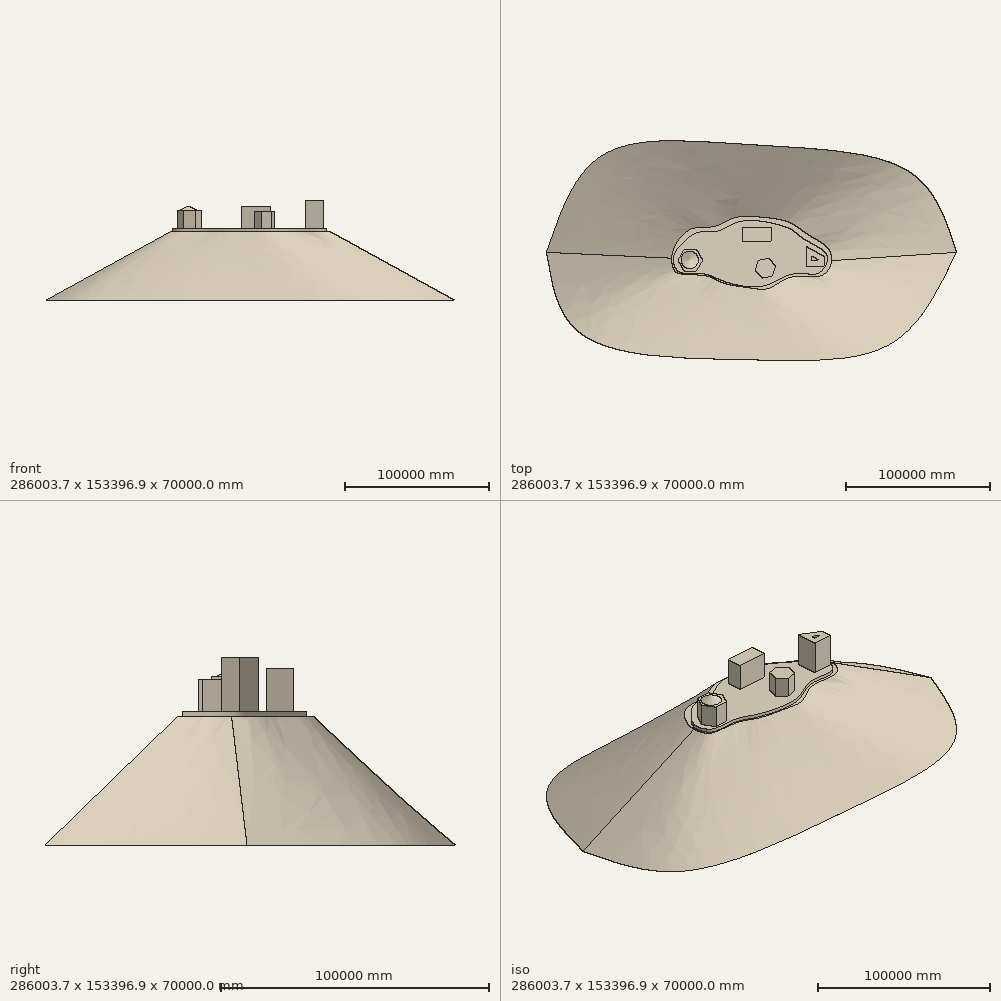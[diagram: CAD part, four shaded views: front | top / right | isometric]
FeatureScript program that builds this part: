
annotation { "Feature Type Name" : "Feature", "Feature Type Description" : "" }
export const myFeature = defineFeature(function(context is Context, id is Id, definition is map)
    precondition{}
    {
        {
            var Q0;
            Q0=qCreatedBy(makeId("Top.planeOp"),FACE);
            var sketch = newSketch(context, id + "F0", { "sketchPlane" : qUnion([Q0])});
            skFitSpline(sketch, "E0", {"points": [v(-143001.83, 0) * mm, v(-103603.63, 67775.48) * mm, v(0, 75000) * mm, v(111116.53, 55565.9) * mm, v(143001.83, 0) * mm], "startDerivative": vector(119090.8, 351106.87) * mm, "endDerivative": vector(96155.49, -304758.65) * mm});
            skFitSpline(sketch, "E1", {"points": [v(-143001.83, 0) * mm, v(-118760.35, -56846.41) * mm, v(0, -75000) * mm, v(98485.93, -63161.72) * mm, v(143001.83, 0) * mm], "startDerivative": vector(50450.26, -316321.73) * mm, "endDerivative": vector(152462.47, 323683.6) * mm});
            skSolve(sketch);
        }
        {
            var Q0;
            Q0=qCreatedBy(makeId("Top.planeOp"),FACE);
            cPlane(context, id + "F1", {"entities" : qUnion([Q0]), "cplaneType" : CPlaneType.OFFSET, "offset" : 48000 * mm, "width" : 150 * mm, "height" : 150 * mm});
        }
        {
            var Q0;
            Q0=qCreatedBy(id+"F1.planeOp",FACE);
            var sketch = newSketch(context, id + "F2", { "sketchPlane" : qUnion([Q0])});
            skFitSpline(sketch, "E2", {"points": [v(-55000, 0) * mm, v(-42253.62, 16006.7) * mm, v(-25722.82, 17990.39) * mm, v(-13159.41, 23610.86) * mm, v(0, 25000) * mm, v(26183.88, 20965.93) * mm, v(39408.52, 12369.92) * mm, v(55000, 0) * mm, v(50649.47, -15401.82) * mm, v(28828.81, -17054.9) * mm, v(12628.63, -24989.68) * mm, v(0, -25000) * mm, v(-20763.58, -21022.3) * mm, v(-31673.9, -16393.67) * mm, v(-51510.86, -14409.97) * mm, v(-55000, -9781.35) * mm, v(-55000, 0) * mm]});
            skSolve(sketch);
        }
        {
            var Q0;
            Q0=makeQuery(id+"F2.imprint","IMPRINT",FACE,{"disambiguationData":[TD([[makeQuery(id+"F2.imprint","IMPRINT",EDGE,{"derivedFrom":sQuery(id+"F2.wireOp",EDGE,"E2")}),-1.0]])]});
            var Q1;
            Q1=makeQuery(id+"F0.imprint","IMPRINT",FACE,{"disambiguationData":[TD([[makeQuery(id+"F0.imprint","IMPRINT",EDGE,{"derivedFrom":sQuery(id+"F0.wireOp",EDGE,"E0")}),-1.0]])]});
            loft(context, id + "F3", {"sheetProfilesArray" : [{ "sheetProfileEntities" : qUnion([Q0]) }, { "sheetProfileEntities" : qUnion([Q1]) }]});
        }
        {
            var Q0;
            Q0=makeQuery(id+"F3.opLoft","CAP_FACE",FACE,{"disambiguationData":[OSD([makeQuery(id+"F2.imprint","IMPRINT",FACE,{"disambiguationData":[TD([[makeQuery(id+"F2.imprint","IMPRINT",EDGE,{"derivedFrom":sQuery(id+"F2.wireOp",EDGE,"E2")}),-1.0]])]})])],"isStart":true});
            var sketch = newSketch(context, id + "F4", { "sketchPlane" : qUnion([Q0])});
            skLineSegment(sketch, "E3.0", {"start": v(-46900.84, 1856.44) * mm, "end": v(-38240.59, 1856.44) * mm});
            skLineSegment(sketch, "E3.1", {"start": v(-38240.59, 1856.44) * mm, "end": v(-33910.46, -5643.56) * mm});
            skLineSegment(sketch, "E3.2", {"start": v(-33910.46, -5643.56) * mm, "end": v(-38240.59, -13143.56) * mm});
            skLineSegment(sketch, "E3.3", {"start": v(-38240.59, -13143.56) * mm, "end": v(-46900.84, -13143.56) * mm});
            skLineSegment(sketch, "E3.4", {"start": v(-46900.84, -13143.56) * mm, "end": v(-51230.97, -5643.56) * mm});
            skLineSegment(sketch, "E3.5", {"start": v(-51230.97, -5643.56) * mm, "end": v(-46900.84, 1856.44) * mm});
            skPoint(sketch, "E3.0.midPoint", {"position": v(-42570.72, 1856.44) * mm});
            skSolve(sketch);
        }
        {
            var Q0;
            Q0=makeQuery(id+"F4.imprint","IMPRINT",FACE,{"disambiguationData":[TD([[makeQuery(id+"F4.imprint","IMPRINT",EDGE,{"derivedFrom":sQuery(id+"F4.wireOp",EDGE,"E3.0")}),-1.0]])]});
            extrude(context, id + "F5", {"entities" : qUnion([Q0]), "operationType" : NewBodyOperationType.ADD, "depth" : 15000 * mm});
        }
        {
            var Q0;
            Q0=makeQuery(id+"F3.opLoft","CAP_FACE",FACE,{"disambiguationData":[OSD([makeQuery(id+"F2.imprint","IMPRINT",FACE,{"disambiguationData":[TD([[makeQuery(id+"F2.imprint","IMPRINT",EDGE,{"derivedFrom":sQuery(id+"F2.wireOp",EDGE,"E2")}),-1.0]])]})])],"isStart":true});
            var sketch = newSketch(context, id + "F6", { "sketchPlane" : qUnion([Q0])});
            skFitSpline(sketch, "E4", {"points": [v(-54539.07, -4369.4) * mm, v(-53149.78, -10690.65) * mm, v(-49607.1, -14024.93) * mm, v(-40159.98, -14719.57) * mm, v(-30296.07, -15622.6) * mm, v(-20223.76, -19859.92) * mm, v(4991.73, -24027.77) * mm, v(19996, -18817.96) * mm, v(31519.21, -14714.38) * mm, v(45049.44, -15130.7) * mm, v(50773.76, -11071.63) * mm, v(52855.34, -2433.1) * mm, v(44945.35, 4540.17) * mm, v(35266.04, 10160.42) * mm, v(28709.09, 15364.35) * mm, v(18925.7, 19319.34) * mm, v(4042.44, 22025.38) * mm, v(-9279.62, 21088.68) * mm, v(-18958.94, 16405.14) * mm, v(-24371.03, 14739.88) * mm, v(-34674.82, 14427.64) * mm, v(-43209.27, 10680.81) * mm, v(-48829.52, 5164.64) * mm, v(-51431.48, 2458.6) * mm, v(-54539.07, -4369.4) * mm]});
            skFitSpline(sketch, "E5.0", {"points": [v(-53544.52, -4476.42) * mm, v(-53547.52, -4499.05) * mm, v(-53550.44, -4521.66) * mm, v(-53554.23, -4551.8) * mm, v(-53558.8, -4589.44) * mm, v(-53564, -4634.58) * mm, v(-53570.55, -4694.73) * mm, v(-53578.03, -4769.84) * mm, v(-53585.88, -4859.82) * mm, v(-53592.64, -4949.67) * mm, v(-53600.18, -5069.29) * mm, v(-53606.92, -5218.46) * mm, v(-53610.77, -5396.9) * mm, v(-53610.48, -5574.73) * mm, v(-53606.15, -5751.95) * mm, v(-53595.12, -5987.4) * mm, v(-53571.67, -6280.03) * mm, v(-53528.82, -6628.25) * mm, v(-53471.97, -6973.25) * mm, v(-53401.87, -7314.66) * mm, v(-53319.26, -7652.1) * mm, v(-53224.9, -7985.19) * mm, v(-53119.6, -8313.47) * mm, v(-53004.11, -8636.52) * mm, v(-52879.3, -8953.87) * mm, v(-52768.19, -9213.19) * mm, v(-52675.48, -9417.32) * mm, v(-52604.15, -9568.7) * mm, v(-52531.13, -9718.31) * mm, v(-52456.52, -9866.08) * mm, v(-52393.12, -9987.64) * mm, v(-52348.14, -10071.87) * mm, v(-52322.28, -10119.76) * mm, v(-52302.8, -10155.55) * mm, v(-52283.25, -10191.2) * mm, v(-52263.62, -10226.75) * mm, v(-52243.95, -10262.1) * mm, v(-52217.66, -10308.96) * mm, v(-52184.7, -10367.08) * mm, v(-52144.94, -10436.05) * mm, v(-52105, -10504.25) * mm, v(-52051.47, -10594.15) * mm, v(-51984.03, -10704.58) * mm, v(-51902.17, -10833.96) * mm, v(-51819.32, -10960.18) * mm, v(-51735.4, -11083.23) * mm, v(-51650.35, -11203.1) * mm, v(-51564.1, -11319.77) * mm, v(-51447.36, -11471.1) * mm, v(-51298.03, -11652.32) * mm, v(-51112.66, -11857.28) * mm, v(-50920.31, -12049.98) * mm, v(-50720.03, -12230.77) * mm, v(-50510.68, -12400.03) * mm, v(-50327.6, -12531.8) * mm, v(-50175.22, -12631.77) * mm, v(-50057.8, -12704.07) * mm, v(-49937.03, -12773.7) * mm, v(-49812.7, -12840.67) * mm, v(-49705.98, -12894.26) * mm, v(-49618.61, -12935.8) * mm, v(-49552.07, -12966.28) * mm, v(-49484.49, -12996.1) * mm, v(-49415.83, -13025.22) * mm, v(-49357.71, -13048.93) * mm, v(-49310.65, -13067.56) * mm, v(-49281, -13079.05) * mm, v(-49257.15, -13088.16) * mm, v(-49233.19, -13097.22) * mm, v(-49203, -13108.45) * mm, v(-49166.44, -13121.77) * mm, v(-49117.22, -13139.34) * mm, v(-49054.8, -13160.92) * mm, v(-48978.54, -13186.22) * mm, v(-48900.9, -13210.91) * mm, v(-48795.58, -13243.02) * mm, v(-48660.6, -13281.64) * mm, v(-48493.46, -13325.52) * mm, v(-48321.32, -13366.96) * mm, v(-48144.34, -13405.96) * mm, v(-47902.13, -13454.74) * mm, v(-47588.1, -13509.74) * mm, v(-47194.53, -13566.53) * mm, v(-46785.56, -13614.53) * mm, v(-46362.45, -13654.23) * mm, v(-45926.46, -13686.23) * mm, v(-45478.78, -13711.12) * mm, v(-45020.6, -13729.57) * mm, v(-44553.06, -13742.26) * mm, v(-44077.28, -13749.9) * mm, v(-43594.36, -13753.22) * mm, v(-43105.36, -13752.94) * mm, v(-42611.34, -13749.83) * mm, v(-42113.32, -13744.64) * mm, v(-41695.81, -13739.23) * mm, v(-41360.8, -13734.64) * mm, v(-41109.17, -13731.16) * mm, v(-40857.28, -13727.75) * mm, v(-40647.26, -13725.04) * mm, v(-40479.23, -13723) * mm, v(-40353.22, -13721.55) * mm, v(-40227.24, -13720.19) * mm, v(-40059.3, -13718.51) * mm, v(-39849.65, -13716.7) * mm, v(-39598.45, -13715.02) * mm, v(-39347.67, -13713.88) * mm, v(-39013.89, -13713.17) * mm, v(-38597.78, -13713.9) * mm, v(-38100.41, -13717.75) * mm, v(-37605.12, -13725) * mm, v(-37112.05, -13736.03) * mm, v(-36457.76, -13756.36) * mm, v(-35646.1, -13793.3) * mm, v(-34843.58, -13848.4) * mm, v(-34207.58, -13905.07) * mm, v(-33733.72, -13954.32) * mm, v(-33263.13, -14010.74) * mm, v(-32795.95, -14074.77) * mm, v(-32332.31, -14146.87) * mm, v(-31872.37, -14227.5) * mm, v(-31492.3, -14302.16) * mm, v(-31190.24, -14366.62) * mm, v(-30964.72, -14417.38) * mm, v(-30740.25, -14470.62) * mm, v(-30554.07, -14517.1) * mm, v(-30405.68, -14555.58) * mm, v(-30294.66, -14585.1) * mm, v(-30183.91, -14615.28) * mm, v(-30101.07, -14638.42) * mm, v(-30045.93, -14654.06) * mm, v(-30009.19, -14664.55) * mm, v(-29944.98, -14683.03) * mm, v(-29853.55, -14709.83) * mm, v(-29744.25, -14742.61) * mm, v(-29635.37, -14776) * mm, v(-29526.88, -14810) * mm, v(-29382.75, -14856.09) * mm, v(-29203.5, -14915.15) * mm, v(-28989.74, -14988.26) * mm, v(-28777.19, -15063.5) * mm, v(-28565.71, -15140.8) * mm, v(-28285, -15246.51) * mm, v(-27936.1, -15383.4) * mm, v(-27519.5, -15554.63) * mm, v(-27103.8, -15732.24) * mm, v(-26687.8, -15915.66) * mm, v(-26270.27, -16104.35) * mm, v(-25849.97, -16297.79) * mm, v(-25425.65, -16495.5) * mm, v(-24996.03, -16697) * mm, v(-24559.84, -16901.86) * mm, v(-24115.8, -17109.65) * mm, v(-23662.6, -17319.95) * mm, v(-23198.98, -17532.35) * mm, v(-22723.63, -17746.45) * mm, v(-22235.26, -17961.86) * mm, v(-21732.57, -18178.17) * mm, v(-21300.66, -18358.86) * mm, v(-20946.68, -18503.46) * mm, v(-20676.81, -18611.9) * mm, v(-20448.13, -18702.19) * mm, v(-20262.84, -18774.36) * mm, v(-20122.67, -18828.45) * mm, v(-20004.85, -18873.49) * mm, v(-19909.97, -18909.5) * mm, v(-19814.69, -18945.48) * mm, v(-19694.74, -18990.45) * mm, v(-19549.5, -19044.37) * mm, v(-19402.98, -19098.25) * mm, v(-19205.91, -19170.02) * mm, v(-18956.44, -19259.58) * mm, v(-18652.2, -19366.75) * mm, v(-18343.2, -19473.57) * mm, v(-18029.6, -19579.96) * mm, v(-17605.5, -19721.18) * mm, v(-17064.55, -19896.36) * mm, v(-16399.15, -20103.97) * mm, v(-15718.57, -20308.5) * mm, v(-15023.88, -20509.5) * mm, v(-14316.14, -20706.53) * mm, v(-13356.52, -20963.33) * mm, v(-12129.69, -21272.15) * mm, v(-10622.28, -21619.71) * mm, v(-9088.1, -21940.75) * mm, v(-7535.59, -22231.77) * mm, v(-5973.22, -22489.32) * mm, v(-4409.5, -22709.98) * mm, v(-2852.93, -22890.34) * mm, v(-1312.11, -23027.06) * mm, v(-48.45, -23101.87) * mm, v(945.9, -23136.64) * mm, v(1682.28, -23149.8) * mm, v(2287.16, -23149.66) * mm, v(2765.25, -23142.71) * mm, v(3120.78, -23134.04) * mm, v(3473.1, -23121.85) * mm, v(3822.1, -23106.1) * mm, v(4110.05, -23090) * mm, v(4338.6, -23075.28) * mm, v(4509.08, -23063.33) * mm, v(4678.62, -23050.46) * mm, v(4819.11, -23038.97) * mm, v(4931, -23029.3) * mm, v(5042.61, -23019.34) * mm, v(5181.57, -23006.29) * mm, v(5347.46, -22989.7) * mm, v(5567.51, -22966.38) * mm, v(5840.46, -22934.95) * mm, v(6164.67, -22893.7) * mm, v(6592.62, -22834.08) * mm, v(7119.58, -22751.08) * mm, v(7739.7, -22638.52) * mm, v(8348.11, -22513.6) * mm, v(8945.34, -22376.9) * mm, v(9727.39, -22179.73) * mm, v(10679.53, -21906.75) * mm, v(11785.41, -21541.33) * mm, v(12858.52, -21142.64) * mm, v(13902.66, -20715.24) * mm, v(14921.55, -20263.71) * mm, v(15918.89, -19792.7) * mm, v(16898.29, -19306.87) * mm, v(17863.36, -18811) * mm, v(18817.74, -18309.94) * mm, v(19765.04, -17808.57) * mm, v(20708.96, -17311.91) * mm, v(21653.37, -16824.93) * mm, v(22602.15, -16352.73) * mm, v(23559.2, -15900.54) * mm, v(24528.39, -15473.74) * mm, v(25513.51, -15077.84) * mm, v(26350.8, -14778.42) * mm, v(27032.17, -14560.07) * mm, v(27549.39, -14407.65) * mm, v(28073.2, -14267.28) * mm, v(28603.97, -14139.73) * mm, v(29052.4, -14044.7) * mm, v(29414.97, -13975.83) * mm, v(29688.87, -13927.83) * mm, v(29964.77, -13883.57) * mm, v(30242.7, -13843.15) * mm, v(30522.73, -13806.66) * mm, v(30757.84, -13779.59) * mm, v(30947.02, -13759.98) * mm, v(31089.44, -13746.31) * mm, v(31208.58, -13735.8) * mm, v(31304.17, -13727.9) * mm, v(31364.03, -13723.2) * mm, v(31412, -13719.57) * mm, v(31448, -13716.9) * mm, v(31484.03, -13714.32) * mm, v(31532.1, -13710.95) * mm, v(31592.22, -13706.92) * mm, v(31688.53, -13700.81) * mm, v(31809.1, -13693.84) * mm, v(31954.08, -13686.5) * mm, v(32099.32, -13680.14) * mm, v(32293.32, -13672.96) * mm, v(32536.42, -13666.35) * mm, v(32829.02, -13661.97) * mm, v(33122.37, -13660.96) * mm, v(33416.38, -13663.1) * mm, v(33809.12, -13669.9) * mm, v(34301.14, -13685.33) * mm, v(34892.4, -13713.34) * mm, v(35483.6, -13749.34) * mm, v(36073.8, -13791.84) * mm, v(36662.02, -13839.37) * mm, v(37247.28, -13890.45) * mm, v(37828.57, -13943.66) * mm, v(38404.84, -13997.55) * mm, v(38975.02, -14050.72) * mm, v(39538, -14101.73) * mm, v(40092.66, -14149.22) * mm, v(40637.83, -14191.8) * mm, v(41172.28, -14228.1) * mm, v(41694.78, -14256.83) * mm, v(42204.03, -14276.66) * mm, v(42698.68, -14286.36) * mm, v(43097.55, -14285) * mm, v(43407.93, -14277.71) * mm, v(43636.16, -14269) * mm, v(43859.66, -14256.95) * mm, v(44078.22, -14241.42) * mm, v(44256.1, -14225.5) * mm, v(44395.74, -14210.94) * mm, v(44499.12, -14199.09) * mm, v(44601.12, -14186.3) * mm, v(44684.96, -14174.86) * mm, v(44751.32, -14165.23) * mm, v(44800.73, -14157.77) * mm, v(44841.6, -14151.35) * mm, v(44874.13, -14146.1) * mm, v(44906.52, -14140.77) * mm, v(44946.83, -14133.94) * mm, v(44994.9, -14125.5) * mm, v(45042.68, -14116.8) * mm, v(45106, -14104.88) * mm, v(45184.42, -14089.36) * mm, v(45277.39, -14069.74) * mm, v(45369.23, -14049.15) * mm, v(45490.22, -14020.4) * mm, v(45638.76, -13982.05) * mm, v(45812.83, -13932.21) * mm, v(45982.9, -13878.6) * mm, v(46149.13, -13821.25) * mm, v(46365.9, -13739.83) * mm, v(46628.17, -13628.8) * mm, v(46930.35, -13480.83) * mm, v(47221.36, -13318) * mm, v(47502.49, -13140.12) * mm, v(47774.9, -12946.9) * mm, v(48039.66, -12738.03) * mm, v(48297.66, -12513.2) * mm, v(48549.69, -12272.13) * mm, v(48796.42, -12014.58) * mm, v(48998.12, -11786.11) * mm, v(49157.4, -11594.99) * mm, v(49275.87, -11447.47) * mm, v(49393.43, -11295.78) * mm, v(49510.13, -11139.93) * mm, v(49606.7, -11006.6) * mm, v(49683.6, -10897.85) * mm, v(49741.1, -10815.27) * mm, v(49798.41, -10731.66) * mm, v(49855.57, -10647.02) * mm, v(49898.32, -10582.77) * mm, v(49926.78, -10539.62) * mm, v(49945.74, -10510.77) * mm, v(49978.87, -10460.08) * mm, v(50026.03, -10387.13) * mm, v(50082.35, -10298.75) * mm, v(50138.38, -10209.56) * mm, v(50212.64, -10089.57) * mm, v(50304.6, -9937.67) * mm, v(50413.37, -9752.48) * mm, v(50520.37, -9564.58) * mm, v(50660.46, -9310.67) * mm, v(50830.24, -8987.4) * mm, v(51024.06, -8591.52) * mm, v(51206.54, -8189.19) * mm, v(51376.32, -7781.9) * mm, v(51532.07, -7371.16) * mm, v(51672.5, -6958.52) * mm, v(51796.34, -6545.53) * mm, v(51902.42, -6133.77) * mm, v(51989.61, -5724.82) * mm, v(52056.89, -5320.27) * mm, v(52103.31, -4921.7) * mm, v(52123.94, -4595.79) * mm, v(52129.25, -4339.51) * mm, v(52127.57, -4149.7) * mm, v(52120.14, -3962.44) * mm, v(52106.92, -3777.86) * mm, v(52087.83, -3596.1) * mm, v(52062.83, -3417.25) * mm, v(52037, -3270.72) * mm, v(52013.34, -3155.04) * mm, v(51994.07, -3069.05) * mm, v(51973.27, -2983.84) * mm, v(51954.66, -2913.49) * mm, v(51939, -2857.6) * mm, v(51926.88, -2815.88) * mm, v(51916.44, -2781.27) * mm, v(51907.9, -2753.69) * mm, v(51901.4, -2733.05) * mm, v(51894.8, -2712.44) * mm, v(51885.84, -2685) * mm, v(51874.38, -2650.73) * mm, v(51860.2, -2609.69) * mm, v(51840.74, -2555.06) * mm, v(51815.34, -2486.96) * mm, v(51783.16, -2405.5) * mm, v(51749.29, -2324.3) * mm, v(51701.86, -2216.33) * mm, v(51638.35, -2081.93) * mm, v(51555.4, -1921.45) * mm, v(51465.75, -1761.71) * mm, v(51369.46, -1602.69) * mm, v(51266.56, -1444.35) * mm, v(51157.15, -1286.7) * mm, v(51002.7, -1077.43) * mm, v(50793.77, -817.63) * mm, v(50518.67, -508.94) * mm, v(50220.31, -203.57) * mm, v(49899.97, 98.25) * mm, v(49559.05, 396.34) * mm, v(49199.03, 690.55) * mm, v(48821.43, 980.8) * mm, v(48427.83, 1267.06) * mm, v(48019.82, 1549.38) * mm, v(47599, 1827.83) * mm, v(47166.97, 2102.54) * mm, v(46725.33, 2373.67) * mm, v(46275.68, 2641.41) * mm, v(45895.62, 2861.9) * mm, v(45589.15, 3036.84) * mm, v(45358.27, 3167.36) * mm, v(45126.58, 3297.22) * mm, v(44932.97, 3404.91) * mm, v(44777.87, 3490.78) * mm, v(44661.46, 3555.04) * mm, v(44564.4, 3608.48) * mm, v(44486.73, 3651.17) * mm, v(44409.05, 3693.81) * mm, v(44312, 3747.01) * mm, v(44156.76, 3831.92) * mm, v(43962.86, 3937.68) * mm, v(43730.45, 4064.02) * mm, v(43498.33, 4189.81) * mm, v(43266.54, 4315.1) * mm, v(42957.98, 4481.54) * mm, v(42573.3, 4688.5) * mm, v(42113.59, 4935.44) * mm, v(41656.08, 5181.24) * mm, v(41201.07, 5426.2) * mm, v(40598.08, 5752.1) * mm, v(39852.03, 6158.87) * mm, v(38971.33, 6648.5) * mm, v(38251.46, 7059.84) * mm, v(37685.15, 7392.19) * mm, v(37265.5, 7643.41) * mm, v(36851.21, 7896.92) * mm, v(36442.58, 8153.05) * mm, v(36107.02, 8368.96) * mm, v(35841.69, 8543.34) * mm, v(35644.29, 8675) * mm, v(35448.52, 8807.56) * mm, v(35286.78, 8918.83) * mm, v(35158.25, 9008.34) * mm, v(35062.28, 9075.73) * mm, v(34966.74, 9143.39) * mm, v(34871.65, 9211.3) * mm, v(34792.78, 9268.13) * mm, v(34729.91, 9313.73) * mm, v(34690.71, 9342.29) * mm, v(34659.41, 9365.17) * mm, v(34628.17, 9388.06) * mm, v(34589.2, 9416.7) * mm, v(34542.59, 9451.12) * mm, v(34480.63, 9497.07) * mm, v(34403.56, 9554.59) * mm, v(34311.63, 9623.76) * mm, v(34220.27, 9693.07) * mm, v(34099.17, 9785.65) * mm, v(33949.13, 9901.66) * mm, v(33711.75, 10087.78) * mm, v(33419.84, 10321.2) * mm, v(33076.4, 10601.9) * mm, v(32739, 10882.6) * mm, v(32406.79, 11162.7) * mm, v(32078.95, 11441.65) * mm, v(31754.65, 11718.88) * mm, v(31433.07, 11993.85) * mm, v(31113.39, 12266.04) * mm, v(30794.78, 12534.95) * mm, v(30476.42, 12800.1) * mm, v(30157.5, 13061) * mm, v(29837.18, 13317.22) * mm, v(29514.67, 13568.32) * mm, v(29243.37, 13772.98) * mm, v(29024.4, 13933.74) * mm, v(28859.09, 14052.8) * mm, v(28692.6, 14170.27) * mm, v(28552.78, 14266.82) * mm, v(28440.23, 14343.23) * mm, v(28355.45, 14400.11) * mm, v(28284.5, 14447.16) * mm, v(28227.53, 14484.59) * mm, v(28184.7, 14512.55) * mm, v(28141.78, 14540.4) * mm, v(28098.72, 14568.16) * mm, v(28055.52, 14595.84) * mm, v(27997.74, 14632.62) * mm, v(27925.18, 14678.39) * mm, v(27837.57, 14732.97) * mm, v(27749.41, 14787.2) * mm, v(27631.15, 14859.06) * mm, v(27481.98, 14948.05) * mm, v(27300.82, 15053.52) * mm, v(27117.52, 15157.68) * mm, v(26932.09, 15260.56) * mm, v(26682, 15396.05) * mm, v(26364.1, 15562.31) * mm, v(25974.19, 15757.02) * mm, v(25575.94, 15947.08) * mm, v(25169.44, 16132.66) * mm, v(24754.77, 16313.91) * mm, v(24191.09, 16550.05) * mm, v(23466.5, 16835.24) * mm, v(22565.76, 17162.89) * mm, v(21789.8, 17424.92) * mm, v(21154.21, 17628.66) * mm, v(20670.23, 17778.7) * mm, v(20179.04, 17926.18) * mm, v(19763.8, 18047.07) * mm, v(19428.13, 18142.69) * mm, v(19174.63, 18213.87) * mm, v(18961.95, 18272.77) * mm, v(18790.96, 18319.65) * mm, v(18662.28, 18354.7) * mm, v(18533.2, 18389.62) * mm, v(18360.56, 18436.02) * mm, v(18143.8, 18493.71) * mm, v(17882.19, 18562.43) * mm, v(17531.42, 18653.34) * mm, v(17089.42, 18765.64) * mm, v(16553.68, 18898.1) * mm, v(16012.95, 19028.2) * mm, v(15285.76, 19198.31) * mm, v(14365.98, 19404.44) * mm, v(13247.67, 19640.5) * mm, v(12117.47, 19864.38) * mm, v(10978.09, 20075.23) * mm, v(9832.21, 20272.2) * mm, v(8682.54, 20454.41) * mm, v(7723.57, 20593.26) * mm, v(6957.2, 20696.12) * mm, v(6383.17, 20769.05) * mm, v(5810.22, 20837.66) * mm, v(5238.7, 20901.84) * mm, v(4763.89, 20951.56) * mm, v(4385.1, 20989) * mm, v(4101.57, 21015.93) * mm, v(3818.65, 21041.66) * mm, v(3536.47, 21066.18) * mm, v(3255.03, 21089.45) * mm, v(2974.34, 21111.43) * mm, v(2694.4, 21132.08) * mm, v(2322.18, 21157.8) * mm, v(1858.83, 21186.47) * mm, v(1305.96, 21215) * mm, v(756.31, 21237.38) * mm, v(209.94, 21253.32) * mm, v(-514.1, 21265.62) * mm, v(-1410.65, 21263.5) * mm, v(-2472.44, 21230.81) * mm, v(-3519.73, 21165.77) * mm, v(-4552.12, 21066.25) * mm, v(-5399.75, 20952.81) * mm, v(-6070.1, 20842.7) * mm, v(-6568.97, 20750.17) * mm, v(-6981.42, 20664.56) * mm, v(-7309.4, 20590.83) * mm, v(-7554.41, 20532.88) * mm, v(-7798.43, 20472.25) * mm, v(-8041.46, 20408.9) * mm, v(-8243.16, 20353.8) * mm, v(-8404.03, 20308.35) * mm, v(-8524.43, 20273.55) * mm, v(-8644.59, 20238.04) * mm, v(-8744.5, 20207.87) * mm, v(-8824.33, 20183.37) * mm, v(-8884.13, 20164.81) * mm, v(-8943.86, 20146.08) * mm, v(-9003.54, 20127.17) * mm, v(-9063.18, 20108.06) * mm, v(-9142.67, 20082.34) * mm, v(-9241.96, 20049.72) * mm, v(-9360.98, 20009.84) * mm, v(-9519.5, 19955.72) * mm, v(-9717.31, 19886.3) * mm, v(-9954.1, 19800.3) * mm, v(-10190.24, 19711.72) * mm, v(-10504.19, 19590.32) * mm, v(-10894.8, 19432.71) * mm, v(-11360.28, 19235.16) * mm, v(-11822.13, 19030.13) * mm, v(-12280.02, 18818.61) * mm, v(-12733.6, 18601.57) * mm, v(-13332.17, 18306.13) * mm, v(-14068, 17927.93) * mm, v(-14785.23, 17544.43) * mm, v(-15346.74, 17238.38) * mm, v(-15761.47, 17010.2) * mm, v(-16169.56, 16784.36) * mm, v(-16570.78, 16561.82) * mm, v(-16964.93, 16343.55) * mm, v(-17351.83, 16130.53) * mm, v(-17668.1, 15958.17) * mm, v(-17917.37, 15823.86) * mm, v(-18102.45, 15725.03) * mm, v(-18255.11, 15644.36) * mm, v(-18376.3, 15580.9) * mm, v(-18466.72, 15533.85) * mm, v(-18556.67, 15487.37) * mm, v(-18646.14, 15441.47) * mm, v(-18735.16, 15396.16) * mm, v(-18853.3, 15336.5) * mm, v(-18999.97, 15263.38) * mm, v(-19174.6, 15177.94) * mm, v(-19348.07, 15094.8) * mm, v(-19578.06, 14987) * mm, v(-19863.63, 14858.02) * mm, v(-20204.76, 14712.48) * mm, v(-20545.8, 14576.28) * mm, v(-20888.12, 14449.54) * mm, v(-21233, 14332.4) * mm, v(-21581.64, 14224.99) * mm, v(-21935.18, 14127.39) * mm, v(-22294.7, 14039.67) * mm, v(-22661.3, 13961.82) * mm, v(-22973.62, 13905.13) * mm, v(-23228.14, 13864.63) * mm, v(-23421.51, 13836.65) * mm, v(-23617.52, 13811.05) * mm, v(-23816.32, 13787.8) * mm, v(-23984.45, 13770.38) * mm, v(-24120.51, 13757.6) * mm, v(-24206.23, 13750.07) * mm, v(-24266.58, 13745.06) * mm, v(-24301.18, 13742.26) * mm, v(-24353.16, 13738.14) * mm, v(-24431.44, 13732.23) * mm, v(-24536.5, 13724.9) * mm, v(-24642.2, 13718.1) * mm, v(-24748.57, 13711.81) * mm, v(-24891.24, 13704.09) * mm, v(-25071.18, 13695.62) * mm, v(-25289.57, 13687.23) * mm, v(-25510.35, 13680.45) * mm, v(-25733.45, 13675.16) * mm, v(-26033.87, 13669.92) * mm, v(-26414.72, 13666.43) * mm, v(-26879.5, 13666.13) * mm, v(-27351.2, 13668.74) * mm, v(-27828.95, 13673.3) * mm, v(-28311.86, 13678.84) * mm, v(-28799, 13684.44) * mm, v(-29289.38, 13689.17) * mm, v(-29782.03, 13692.12) * mm, v(-30275.93, 13692.38) * mm, v(-30770.06, 13689.04) * mm, v(-31263.36, 13681.22) * mm, v(-31754.75, 13668.05) * mm, v(-32243.16, 13648.67) * mm, v(-32646.75, 13626.63) * mm, v(-32967, 13605.05) * mm, v(-33205.76, 13586.8) * mm, v(-33442.91, 13566.38) * mm, v(-33678.34, 13543.68) * mm, v(-33872.96, 13522.8) * mm, v(-34027.64, 13504.86) * mm, v(-34143.13, 13490.78) * mm, v(-34258.08, 13476.06) * mm, v(-34372.47, 13460.7) * mm, v(-34457.83, 13448.68) * mm, v(-34514.55, 13440.45) * mm, v(-34552.3, 13434.92) * mm, v(-34599.44, 13427.88) * mm, v(-34655.89, 13419.27) * mm, v(-34731, 13407.56) * mm, v(-34862.07, 13386.45) * mm, v(-35048.22, 13354.57) * mm, v(-35269.86, 13313.56) * mm, v(-35489.78, 13269.83) * mm, v(-35708.01, 13223.4) * mm, v(-35996.76, 13157.89) * mm, v(-36353.56, 13069.34) * mm, v(-36775.28, 12952.55) * mm, v(-37190.72, 12825.37) * mm, v(-37736.47, 12642.12) * mm, v(-38403.77, 12387.76) * mm, v(-39181.92, 12043) * mm, v(-39812.51, 11723.56) * mm, v(-40306.8, 11449.15) * mm, v(-40672.56, 11234.02) * mm, v(-41033.48, 11009.69) * mm, v(-41389.67, 10776.25) * mm, v(-41741.25, 10533.82) * mm, v(-42030.47, 10324.4) * mm, v(-42231, 10173.97) * mm, v(-42345.04, 10086.91) * mm, v(-42430.3, 10021.08) * mm, v(-42501.13, 9965.77) * mm, v(-42557.66, 9921.26) * mm, v(-42599.99, 9887.74) * mm, v(-42642.26, 9854.07) * mm, v(-42698.56, 9808.98) * mm, v(-42768.81, 9752.27) * mm, v(-42852.9, 9683.67) * mm, v(-42964.73, 9591.48) * mm, v(-43103.97, 9474.95) * mm, v(-43270.14, 9333.21) * mm, v(-43490.4, 9141.88) * mm, v(-43763.22, 8898.68) * mm, v(-44086.26, 8601.6) * mm, v(-44404.68, 8300.5) * mm, v(-44718.2, 7996.56) * mm, v(-45026.57, 7691) * mm, v(-45329.53, 7385.03) * mm, v(-45626.86, 7079.82) * mm, v(-45918.36, 6776.56) * mm, v(-46203.82, 6476.43) * mm, v(-46483.08, 6180.59) * mm, v(-46756, 5890.17) * mm, v(-47022.43, 5606.3) * mm, v(-47282.32, 5330.08) * mm, v(-47493.38, 5107.16) * mm, v(-47658.95, 4933.7) * mm, v(-47761.06, 4827.42) * mm, v(-47841.95, 4743.74) * mm, v(-47902.2, 4681.66) * mm, v(-47962.06, 4620.28) * mm, v(-48011.62, 4569.73) * mm, v(-48051.06, 4529.65) * mm, v(-48080.55, 4499.77) * mm, v(-48105.04, 4475.03) * mm, v(-48124.6, 4455.33) * mm, v(-48144.09, 4435.7) * mm, v(-48168.36, 4411.33) * mm, v(-48207, 4372.66) * mm, v(-48254.9, 4324.91) * mm, v(-48311.77, 4268.53) * mm, v(-48368.05, 4213.03) * mm, v(-48423.74, 4158.39) * mm, v(-48497.2, 4086.6) * mm, v(-48587.62, 3998.83) * mm, v(-48693.9, 3896.33) * mm, v(-48798.03, 3796.4) * mm, v(-48900.12, 3698.74) * mm, v(-49000.24, 3603.06) * mm, v(-49131.28, 3477.74) * mm, v(-49290.72, 3324.56) * mm, v(-49476.18, 3143.78) * mm, v(-49657.06, 2963.4) * mm, v(-49834.85, 2780.61) * mm, v(-49981.79, 2623.86) * mm, v(-50099.46, 2494.3) * mm, v(-50187.98, 2394.64) * mm, v(-50276.97, 2292.13) * mm, v(-50366.65, 2186.37) * mm, v(-50442.11, 2095.2) * mm, v(-50503.02, 2020.25) * mm, v(-50548.99, 1962.98) * mm, v(-50587.55, 1914.34) * mm, v(-50618.58, 1874.86) * mm, v(-50641.93, 1844.95) * mm, v(-50665.38, 1814.73) * mm, v(-50696.77, 1774.03) * mm, v(-50736.24, 1722.39) * mm, v(-50783.95, 1659.21) * mm, v(-50847.99, 1573.4) * mm, v(-50928.75, 1463.25) * mm, v(-51026.6, 1326.63) * mm, v(-51125.2, 1185.76) * mm, v(-51224.3, 1040.81) * mm, v(-51356.9, 842.37) * mm, v(-51522.95, 585.04) * mm, v(-51721.2, 262.8) * mm, v(-51916.89, -71.47) * mm, v(-52108.56, -416.39) * mm, v(-52294.75, -770.55) * mm, v(-52474, -1132.53) * mm, v(-52644.89, -1500.93) * mm, v(-52806.02, -1874.3) * mm, v(-52956.02, -2251.16) * mm, v(-53093.56, -2630.03) * mm, v(-53196.69, -2946.16) * mm, v(-53271.69, -3198.53) * mm, v(-53324.03, -3387.35) * mm, v(-53372.32, -3575.5) * mm, v(-53416.42, -3762.8) * mm, v(-53449.56, -3918) * mm, v(-53473.85, -4041.52) * mm, v(-53490.94, -4133.82) * mm, v(-53506.88, -4225.76) * mm, v(-53519.2, -4302.05) * mm, v(-53528.47, -4362.87) * mm, v(-53535.13, -4408.38) * mm, v(-53540.43, -4446.21) * mm, v(-53544.52, -4476.42) * mm, v(-53547.52, -4499.05) * mm, v(-53550.44, -4521.66) * mm, v(-53544.52, -4476.42) * mm]});
            skSolve(sketch);
        }
        {
            var Q0;
            Q0=makeQuery(id+"F6.imprint","IMPRINT",FACE,{"disambiguationData":[TD([[makeQuery(id+"F6.imprint","IMPRINT",EDGE,{"derivedFrom":sQuery(id+"F6.wireOp",EDGE,"E4")}),1.0]])]});
            extrude(context, id + "F7", {"entities" : qUnion([Q0]), "operationType" : NewBodyOperationType.ADD, "depth" : 2000 * mm});
        }
        {
            var Q0;
            Q0=makeQuery(id+"F7.boolean.opBoolean","SPLIT",FACE,{"disambiguationData":[TD([makeQuery(id+"F5.opExtrude","SWEPT_FACE",FACE,{"disambiguationData":[OSD([sQuery(id+"F4.wireOp",EDGE,"E3.0")])]})])],"derivedFrom":makeQuery(id+"F3.opLoft","CAP_FACE",FACE,{"disambiguationData":[OSD([makeQuery(id+"F2.imprint","IMPRINT",FACE,{"disambiguationData":[TD([[makeQuery(id+"F2.imprint","IMPRINT",EDGE,{"derivedFrom":sQuery(id+"F2.wireOp",EDGE,"E2")}),-1.0]])]})])],"isStart":true})});
            var sketch = newSketch(context, id + "F8", { "sketchPlane" : qUnion([Q0])});
            skCircle(sketch, "E6.cCircle", {"center": v(9728.9, -11094.22) * mm, "radius": 6341.06 * mm, "construction": true});
            skLineSegment(sketch, "E6.0", {"start": v(7561.32, -18088.04) * mm, "end": v(2588.28, -12713.95) * mm});
            skLineSegment(sketch, "E6.1", {"start": v(2588.28, -12713.95) * mm, "end": v(4755.86, -5720.13) * mm});
            skLineSegment(sketch, "E6.2", {"start": v(4755.86, -5720.13) * mm, "end": v(11896.48, -4100.4) * mm});
            skLineSegment(sketch, "E6.3", {"start": v(11896.48, -4100.4) * mm, "end": v(16869.52, -9474.48) * mm});
            skLineSegment(sketch, "E6.4", {"start": v(16869.52, -9474.48) * mm, "end": v(14701.94, -16468.3) * mm});
            skLineSegment(sketch, "E6.5", {"start": v(14701.94, -16468.3) * mm, "end": v(7561.32, -18088.04) * mm});
            skPoint(sketch, "E6.0.midPoint", {"position": v(5074.8, -15401) * mm});
            skSolve(sketch);
        }
        {
            var Q0;
            Q0=makeQuery(id+"F8.imprint","IMPRINT",FACE,{"disambiguationData":[TD([[makeQuery(id+"F8.imprint","IMPRINT",EDGE,{"derivedFrom":sQuery(id+"F8.wireOp",EDGE,"E6.0")}),-1.0]])]});
            extrude(context, id + "F9", {"entities" : qUnion([Q0]), "operationType" : NewBodyOperationType.ADD, "depth" : 14000 * mm});
        }
        {
            var Q0;
            Q0=makeQuery(id+"F7.boolean.opBoolean","SPLIT",FACE,{"disambiguationData":[TD([makeQuery(id+"F5.opExtrude","SWEPT_FACE",FACE,{"disambiguationData":[OSD([sQuery(id+"F4.wireOp",EDGE,"E3.0")])]})])],"derivedFrom":makeQuery(id+"F3.opLoft","CAP_FACE",FACE,{"disambiguationData":[OSD([makeQuery(id+"F2.imprint","IMPRINT",FACE,{"disambiguationData":[TD([[makeQuery(id+"F2.imprint","IMPRINT",EDGE,{"derivedFrom":sQuery(id+"F2.wireOp",EDGE,"E2")}),-1.0]])]})])],"isStart":true})});
            var sketch = newSketch(context, id + "F10", { "sketchPlane" : qUnion([Q0])});
            skLineSegment(sketch, "E7", {"start": v(38056.27, 4180.43) * mm, "end": v(50587.01, -2805.73) * mm});
            skLineSegment(sketch, "E8", {"start": v(50587.01, -2805.73) * mm, "end": v(50587.01, -9663.03) * mm});
            skLineSegment(sketch, "E9", {"start": v(50587.01, -9663.03) * mm, "end": v(38056.27, -9663.03) * mm});
            skLineSegment(sketch, "E10", {"start": v(38056.27, -9663.03) * mm, "end": v(38056.27, 4180.43) * mm});
            skLineSegment(sketch, "E11.0", {"start": v(42056.27, -2629.32) * mm, "end": v(46587.01, -5155.3) * mm});
            skLineSegment(sketch, "E11.1", {"start": v(42056.27, -5663.03) * mm, "end": v(42056.27, -2629.32) * mm});
            skLineSegment(sketch, "E11.2", {"start": v(46587.01, -5663.03) * mm, "end": v(42056.27, -5663.03) * mm});
            skLineSegment(sketch, "E11.3", {"start": v(46587.01, -5155.3) * mm, "end": v(46587.01, -5663.03) * mm});
            skSolve(sketch);
        }
        {
            var Q0;
            {var subQ5=sQuery(id+"F10.wireOp",EDGE,"E7");Q0=makeQuery(id+"F10.imprint","IMPRINT",FACE,{"disambiguationData":[TD([[makeQuery(id+"F10.imprint","IMPRINT",EDGE,{"derivedFrom":subQ5}),-1.0]])]});}
            extrude(context, id + "F11", {"entities" : qUnion([Q0]), "operationType" : NewBodyOperationType.ADD, "depth" : 22000 * mm});
        }
        {
            var Q0;
            Q0=makeQuery(id+"F5.opExtrude","CAP_FACE",FACE,{"disambiguationData":[OSD([sQuery(id+"F4.wireOp",EDGE,"E3.0"),sQuery(id+"F4.wireOp",EDGE,"E3.1"),sQuery(id+"F4.wireOp",EDGE,"E3.2"),sQuery(id+"F4.wireOp",EDGE,"E3.3"),sQuery(id+"F4.wireOp",EDGE,"E3.4"),sQuery(id+"F4.wireOp",EDGE,"E3.5")])],"isStart":false});
            cPlane(context, id + "F12", {"entities" : qUnion([Q0]), "cplaneType" : CPlaneType.OFFSET, "offset" : 3000 * mm, "width" : 150 * mm, "height" : 150 * mm});
        }
        {
            var Q0;
            Q0=qCreatedBy(id+"F12.planeOp",FACE);
            var sketch = newSketch(context, id + "F13", { "sketchPlane" : qUnion([Q0])});
            skCircle(sketch, "E12", {"center": v(-42982.9, -5402.65) * mm, "radius": 250 * mm});
            skSolve(sketch);
        }
        {
            var Q0;
            Q0=makeQuery(id+"F5.opExtrude","CAP_FACE",FACE,{"disambiguationData":[OSD([sQuery(id+"F4.wireOp",EDGE,"E3.0"),sQuery(id+"F4.wireOp",EDGE,"E3.1"),sQuery(id+"F4.wireOp",EDGE,"E3.2"),sQuery(id+"F4.wireOp",EDGE,"E3.3"),sQuery(id+"F4.wireOp",EDGE,"E3.4"),sQuery(id+"F4.wireOp",EDGE,"E3.5")])],"isStart":false});
            var sketch = newSketch(context, id + "F14", { "sketchPlane" : qUnion([Q0])});
            skCircle(sketch, "E13", {"center": v(-42988.3, -5345.05) * mm, "radius": 6045 * mm});
            skSolve(sketch);
        }
        {
            var Q1;
            Q1=makeQuery(id+"F14.imprint","IMPRINT",FACE,{"disambiguationData":[TD([[makeQuery(id+"F14.imprint","IMPRINT",EDGE,{"derivedFrom":sQuery(id+"F14.wireOp",EDGE,"E13")}),1.0]])]});
            var Q2;
            Q2=sQuery(id+"F13.wireOp",VERTEX,"E12.center");
            loft(context, id + "F15", {"operationType" : NewBodyOperationType.ADD, "sheetProfilesArray" : [{ "sheetProfileEntities" : qUnion([Q1]) }, { "sheetProfileEntities" : qUnion([Q2]) }]});
        }
        {
            var Q0;
            {var subQ4=makeQuery(id+"F5.opExtrude","SWEPT_FACE",FACE,{"disambiguationData":[OSD([sQuery(id+"F4.wireOp",EDGE,"E3.0")])]});Q0=makeQuery(id+"F11.boolean.opBoolean","SPLIT",FACE,{"disambiguationData":[TD([subQ4])],"derivedFrom":makeQuery(id+"F7.boolean.opBoolean","SPLIT",FACE,{"disambiguationData":[TD([subQ4])],"derivedFrom":makeQuery(id+"F3.opLoft","CAP_FACE",FACE,{"disambiguationData":[OSD([makeQuery(id+"F2.imprint","IMPRINT",FACE,{"disambiguationData":[TD([[makeQuery(id+"F2.imprint","IMPRINT",EDGE,{"derivedFrom":sQuery(id+"F2.wireOp",EDGE,"E2")}),-1.0]])]})])],"isStart":true})})});}
            var sketch = newSketch(context, id + "F16", { "sketchPlane" : qUnion([Q0])});
            skLineSegment(sketch, "E14.bottom", {"start": v(-6383.37, 17461.39) * mm, "end": v(13616.63, 17461.39) * mm});
            skLineSegment(sketch, "E14.top", {"start": v(-6383.37, 7461.39) * mm, "end": v(13616.63, 7461.39) * mm});
            skLineSegment(sketch, "E14.left", {"start": v(-6383.37, 17461.39) * mm, "end": v(-6383.37, 7461.39) * mm});
            skLineSegment(sketch, "E14.right", {"start": v(13616.63, 17461.39) * mm, "end": v(13616.63, 7461.39) * mm});
            skSolve(sketch);
        }
        {
            var Q0;
            Q0=makeQuery(id+"F16.imprint","IMPRINT",FACE,{"disambiguationData":[TD([[makeQuery(id+"F16.imprint","IMPRINT",EDGE,{"derivedFrom":sQuery(id+"F16.wireOp",EDGE,"E14.bottom")}),-1.0]])]});
            extrude(context, id + "F17", {"entities" : qUnion([Q0]), "operationType" : NewBodyOperationType.ADD, "depth" : 18000 * mm});
        }
    });
